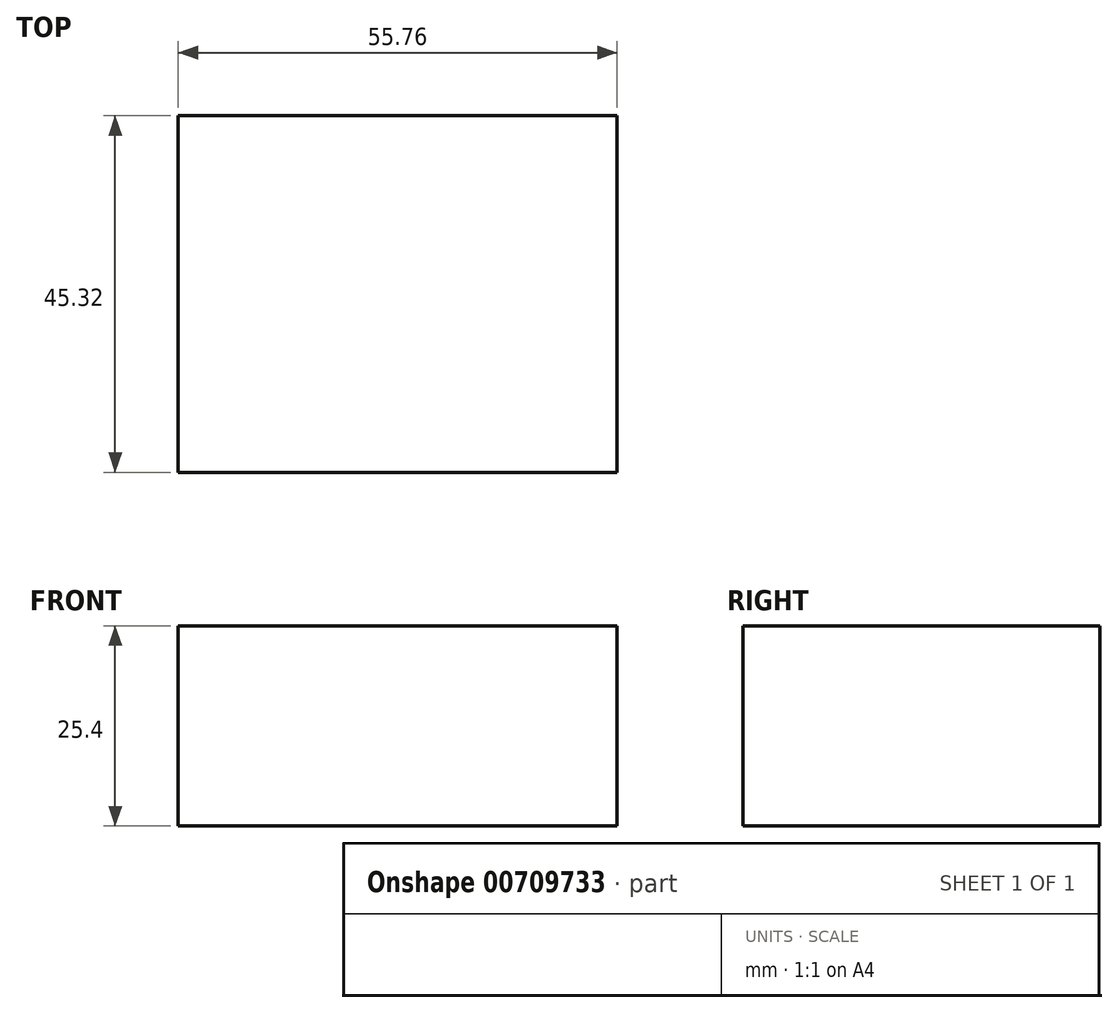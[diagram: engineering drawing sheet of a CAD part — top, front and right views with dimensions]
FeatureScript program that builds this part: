
annotation { "Feature Type Name" : "Feature", "Feature Type Description" : "" }
export const myFeature = defineFeature(function(context is Context, id is Id, definition is map)
    precondition{}
    {
        {
            var Q0;
            Q0=qCreatedBy(makeId("Top.planeOp"),FACE);
            var sketch = newSketch(context, id + "F0", { "sketchPlane" : qUnion([Q0])});
            skLineSegment(sketch, "E0.bottom", {"start": v(-27.88, -22.66) * mm, "end": v(27.88, -22.66) * mm});
            skLineSegment(sketch, "E0.top", {"start": v(-27.88, 22.66) * mm, "end": v(27.88, 22.66) * mm});
            skLineSegment(sketch, "E0.left", {"start": v(-27.88, -22.66) * mm, "end": v(-27.88, 22.66) * mm});
            skLineSegment(sketch, "E0.right", {"start": v(27.88, -22.66) * mm, "end": v(27.88, 22.66) * mm});
            skPoint(sketch, "E0.middle", {"position": v(0, 0) * mm});
            skSolve(sketch);
        }
        {
            var Q0;
            Q0 = qSketchRegion(id + "F0", true);
            extrude(context, id + "F1", {"entities" : qUnion([Q0]), "depth" : 25.4 * mm, "offsetDistance" : 25.4 * mm});
        }
    });
